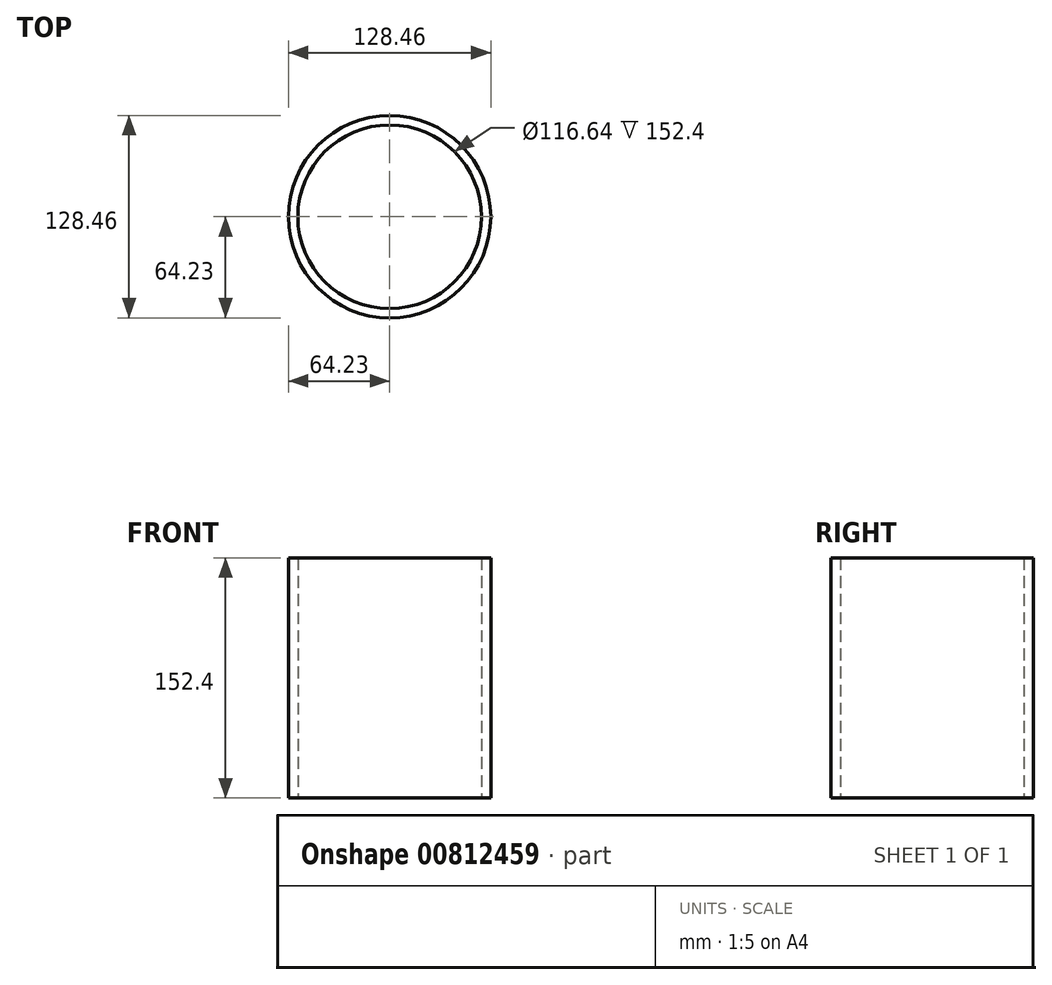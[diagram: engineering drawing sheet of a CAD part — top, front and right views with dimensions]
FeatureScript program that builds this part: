
annotation { "Feature Type Name" : "Feature", "Feature Type Description" : "" }
export const myFeature = defineFeature(function(context is Context, id is Id, definition is map)
    precondition{}
    {
        {
            var Q0;
            Q0=qCreatedBy(makeId("Top.planeOp"),FACE);
            var sketch = newSketch(context, id + "F0", { "sketchPlane" : qUnion([Q0])});
            skCircle(sketch, "E0", {"center": v(0, 0) * mm, "radius": 64.23 * mm});
            skCircle(sketch, "E1", {"center": v(0, 0) * mm, "radius": 58.32 * mm});
            skSolve(sketch);
        }
        {
            var Q0;
            Q0=makeQuery(id+"F0.imprint","IMPRINT",FACE,{"disambiguationData":[TD([[makeQuery(id+"F0.imprint","IMPRINT",EDGE,{"derivedFrom":sQuery(id+"F0.wireOp",EDGE,"E0")}),1.0]])]});
            extrude(context, id + "F1", {"entities" : qUnion([Q0]), "endBound" : BoundingType.SYMMETRIC, "depth" : 152.4 * mm, "offsetDistance" : 25.4 * mm});
        }
    });
